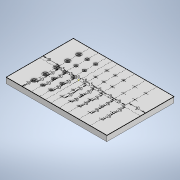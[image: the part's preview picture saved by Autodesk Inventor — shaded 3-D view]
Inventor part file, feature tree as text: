
AUTODESK INVENTOR PART (.ipt)
format: ipt  version: 2020.3 (Build 243373000, 373)  size: 211,968 bytes
history: native  units: mm
features: hole x25, sketch x1, extrude x1
ambient origin geometry x8: Origin, YZ Plane, XZ Plane, XY Plane, X Axis, Y Axis, Z Axis, Center Point
bodies: Solid1 (feature_tree)
feature tree (27):
  sketch  "Sketch1"  dims[d6=10.0mm d8=15.0mm d9=15.0mm d10=30.0mm d11=10.0mm d12=15.0mm d13=15.0mm d14=20.0mm d15=20.0mm d16=30.0mm d17=20.0mm d18=20.0mm d19=20.0mm d22=20.0mm d23=20.0mm d24=20.0mm d25=20.0mm d29=20.0mm d30=20.0mm d31=20.0mm d32=20.0mm d33=20.0mm d34=20.0mm d35=20.0mm d36=20.0mm d37=20.0mm d38=20.0mm d39=10.0mm d40=0.0mm d41=5.6mm d42=6.0mm d43=9.0mm d44=1.0mm d45=90.0deg d46=6.5mm d47=0.0mm d48=5.6mm d49=6.0mm d50=9.0mm d51=1.0mm d52=90.0deg d53=6.5mm d54=0.0mm d55=5.8mm d56=6.0mm d57=9.0mm d58=1.0mm d59=90.0deg d60=6.5mm d61=0.0mm d62=5.8mm d63=6.0mm d64=9.0mm d65=1.0mm d66=90.0deg d67=6.5mm d68=0.0mm d69=5.9mm d70=6.0mm d71=9.0mm d72=1.0mm d73=90.0deg d74=6.5mm d75=0.0mm d76=5.9mm d77=6.0mm d78=9.0mm d79=1.0mm d80=90.0deg d81=6.5mm d82=0.0mm d83=6.0mm d84=6.0mm d85=9.0mm d86=1.0mm d87=90.0deg d88=6.5mm d89=0.0mm d90=6.0mm d91=6.0mm d92=9.0mm d93=1.0mm d94=90.0deg d95=6.5mm d96=0.0mm d97=6.2mm d98=6.0mm d99=9.0mm d100=1.0mm d101=90.0deg d102=6.5mm d103=0.0mm d104=6.2mm d105=6.0mm d106=9.0mm d107=1.0mm d108=90.0deg d109=6.5mm d110=0.0mm d111=2.2mm d112=6.0mm d113=9.0mm d114=1.0mm d115=90.0deg d116=6.5mm d117=0.0mm d118=2.0mm d119=6.0mm d120=9.0mm d121=1.0mm d122=90.0deg d123=6.5mm d124=0.0mm d125=1.9mm d126=6.0mm d127=9.0mm d128=1.0mm d129=90.0deg d130=6.5mm d131=0.0mm d132=1.8mm d133=6.0mm d134=9.0mm d135=1.0mm d136=90.0deg d137=6.5mm d138=0.0mm d139=1.6mm d140=6.0mm d141=9.0mm d142=1.0mm d143=90.0deg d144=6.5mm d145=0.0mm d146=1.6mm d147=6.0mm d148=9.0mm d149=1.0mm d150=90.0deg d151=6.5mm d152=0.0mm d153=1.7mm d154=6.0mm d155=9.0mm d156=1.0mm d157=90.0deg d158=6.5mm d159=0.0mm d160=1.8mm d161=6.0mm d162=9.0mm d163=1.0mm d164=90.0deg d165=6.5mm d166=0.0mm d167=1.9mm d168=6.0mm d169=9.0mm d170=1.0mm d171=90.0deg d172=6.5mm d173=0.0mm d174=2.0mm d175=6.0mm d176=9.0mm d177=1.0mm d178=90.0deg d179=6.5mm d180=0.0mm d181=3.0mm d182=6.0mm d183=9.0mm d184=1.0mm d185=90.0deg d186=3.2mm d187=0.0mm d188=3.1mm d189=6.0mm d190=9.0mm d191=1.0mm d192=90.0deg d193=3.2mm d194=0.0mm d195=3.2mm d196=6.0mm d197=9.0mm d198=1.0mm d199=90.0deg d200=3.2mm d201=0.0mm d202=3.3mm d203=6.0mm d204=9.0mm d205=1.0mm d206=90.0deg d207=3.2mm d208=0.0mm d209=2.9mm d210=6.0mm d211=9.0mm d212=1.0mm d213=90.0deg d214=3.2mm d215=0.0mm]
  extrude  "Extrusion1"  Depth=3.2mm
  hole  "Hole1"  [1 undecoded]
  hole  "Hole2"  [1 undecoded]
  hole  "Hole3"  [1 undecoded]
  hole  "Hole4"  [1 undecoded]
  hole  "Hole5"  [1 undecoded]
  hole  "Hole6"  [1 undecoded]
  hole  "Hole7"  [1 undecoded]
  hole  "Hole8"  [1 undecoded]
  hole  "Hole9"  [1 undecoded]
  hole  "Hole10"  [1 undecoded]
  hole  "Hole11"  [1 undecoded]
  hole  "Hole12"  [1 undecoded]
  hole  "Hole13"  [1 undecoded]
  hole  "Hole14"  [1 undecoded]
  hole  "Hole15"  [1 undecoded]
  hole  "Hole16"  [1 undecoded]
  hole  "Hole17"  [1 undecoded]
  hole  "Hole18"  [1 undecoded]
  hole  "Hole19"  [1 undecoded]
  hole  "Hole20"  [1 undecoded]
  hole  "Hole21"  [1 undecoded]
  hole  "Hole22"  [1 undecoded]
  hole  "Hole23"  [1 undecoded]
  hole  "Hole24"  [1 undecoded]
  hole  "Hole25"  [1 undecoded]
note: 25 required parameter values undecoded (feature->parameter linkage not recoverable at this tier; creation-order binding heuristic only, values carry confidence <= 0.55)
